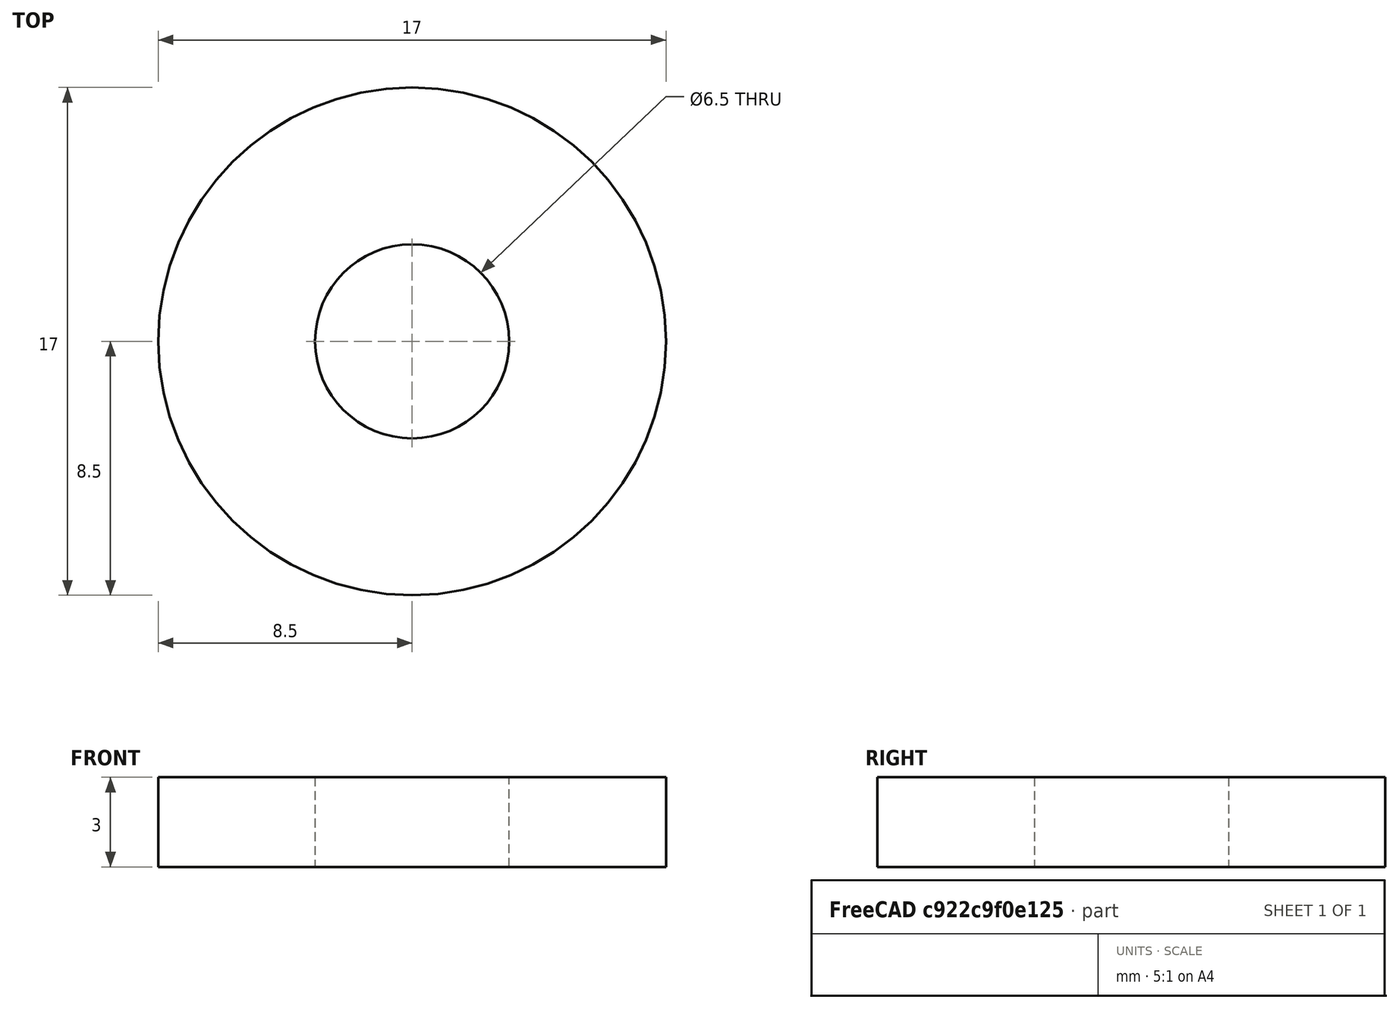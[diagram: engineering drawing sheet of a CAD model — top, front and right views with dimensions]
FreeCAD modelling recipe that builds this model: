
FCSTD DOCUMENT  (FreeCAD 0.20R29603 (Git))
Label: Washer
License: All rights reserved
LicenseURL: http://en.wikipedia.org/wiki/All_rights_reserved
objects: Sketcher::SketchObject×1, PartDesign::Pad×1, PartDesign::Body×1
note: 4 computed .brp shape members not serialized (recipe doc carries the construction recipe); baked Part::Feature solids carry a one-line shape summary decoded from their .brp

FEATURE [Sketcher::SketchObject] Sketch
  FullyConstrained = true
  MapMode = 5
  Support = -> [XY_Plane]
  sketch-geometry (2):
    g0: Circle CenterX=0 CenterY=0 CenterZ=0 NormalX=0 NormalY=0 NormalZ=1 AngleXU=0 Radius=3.25
    g1: Circle CenterX=0 CenterY=0 CenterZ=0 NormalX=0 NormalY=0 NormalZ=1 AngleXU=0 Radius=8.5
  constraints (4):
    c: Coincident(g0,g-1)
    c: Coincident(g1,g0)
    c: Diameter(g0) = 6.5
    c: Diameter(g1) = 17
FEATURE [PartDesign::Pad] Pad
  Direction = (0,0,1)
  Length = 3
  Length2 = 10
  Profile = -> Sketch
  ReferenceAxis = -> Sketch [N_Axis]
  Type = 0
FEATURE [PartDesign::Body] Body
  Group = -> [Sketch,Pad]
  Origin = -> Origin
  Tip = -> Pad
